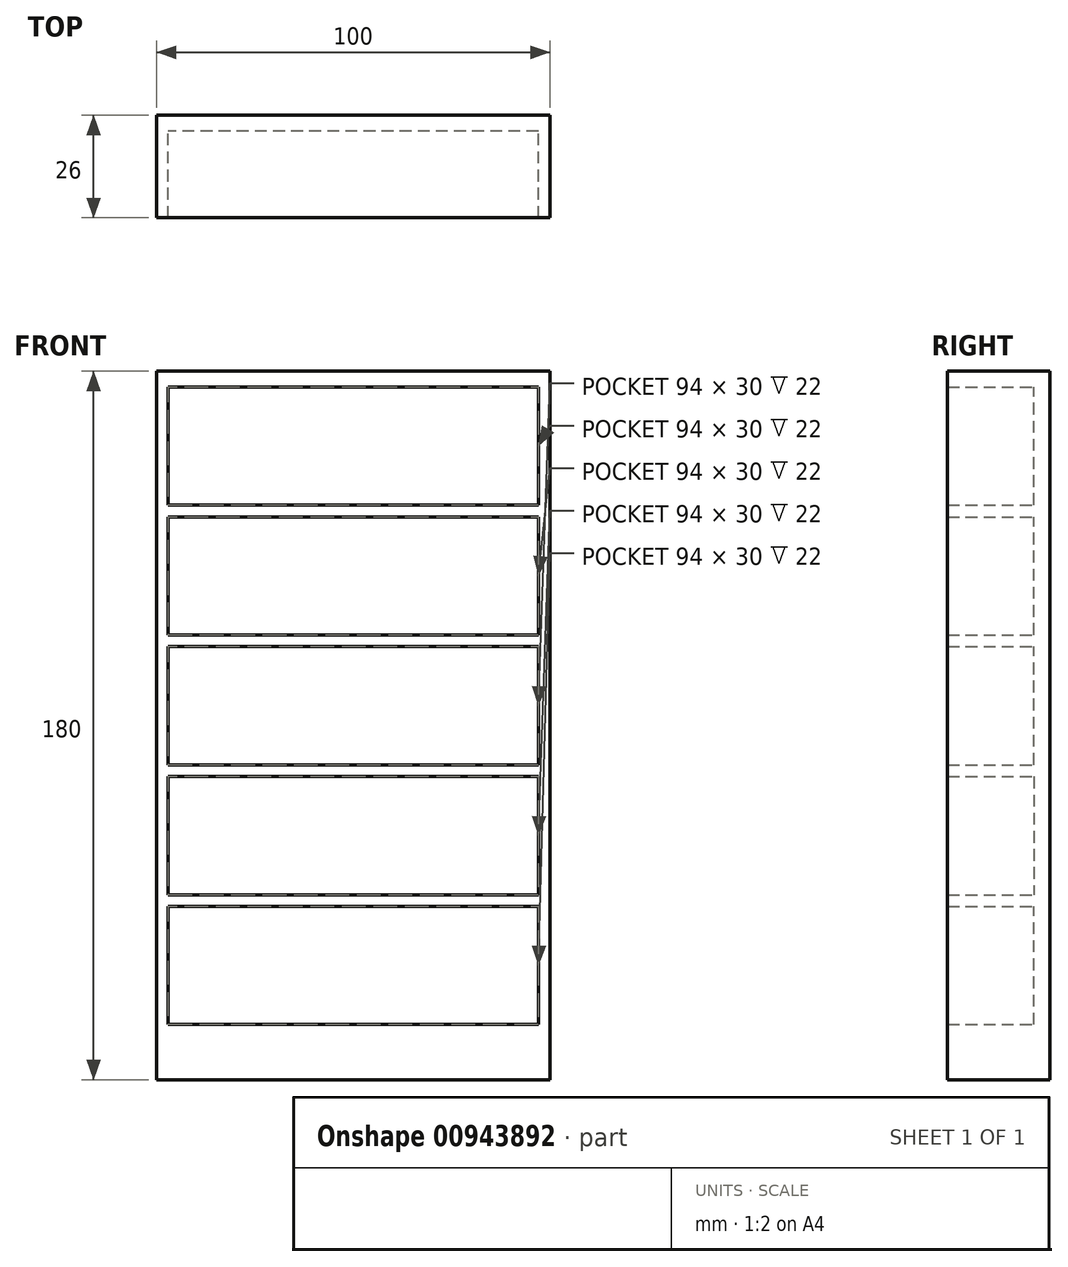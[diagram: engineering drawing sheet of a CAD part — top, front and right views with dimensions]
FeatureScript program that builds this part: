
annotation { "Feature Type Name" : "Feature", "Feature Type Description" : "" }
export const myFeature = defineFeature(function(context is Context, id is Id, definition is map)
    precondition{}
    {
        {
            var Q0;
            Q0=qCreatedBy(makeId("Front.planeOp"),FACE);
            var sketch = newSketch(context, id + "F0", { "sketchPlane" : qUnion([Q0])});
            skLineSegment(sketch, "E0.bottom", {"start": v(50, 90) * mm, "end": v(-50, 90) * mm});
            skLineSegment(sketch, "E0.top", {"start": v(50, -90) * mm, "end": v(-50, -90) * mm});
            skLineSegment(sketch, "E0.left", {"start": v(50, 90) * mm, "end": v(50, -90) * mm});
            skLineSegment(sketch, "E0.right", {"start": v(-50, 90) * mm, "end": v(-50, -90) * mm});
            skPoint(sketch, "E0.middle", {"position": v(0, 0) * mm});
            skLineSegment(sketch, "E1.bottom", {"start": v(-47, 86) * mm, "end": v(47, 86) * mm});
            skLineSegment(sketch, "E1.top", {"start": v(-47, 56) * mm, "end": v(47, 56) * mm});
            skLineSegment(sketch, "E1.left", {"start": v(-47, 86) * mm, "end": v(-47, 56) * mm});
            skLineSegment(sketch, "E1.right", {"start": v(47, 86) * mm, "end": v(47, 56) * mm});
            skLineSegment(sketch, "E2.bottom", {"start": v(-47, 53) * mm, "end": v(47, 53) * mm});
            skLineSegment(sketch, "E2.top", {"start": v(-47, 23) * mm, "end": v(47, 23) * mm});
            skLineSegment(sketch, "E2.left", {"start": v(-47, 53) * mm, "end": v(-47, 23) * mm});
            skLineSegment(sketch, "E2.right", {"start": v(47, 53) * mm, "end": v(47, 23) * mm});
            skLineSegment(sketch, "E3.bottom", {"start": v(-47, 20) * mm, "end": v(47, 20) * mm});
            skLineSegment(sketch, "E3.top", {"start": v(-47, -10) * mm, "end": v(47, -10) * mm});
            skLineSegment(sketch, "E3.left", {"start": v(47, 20) * mm, "end": v(47, -10) * mm});
            skLineSegment(sketch, "E3.right", {"start": v(-47, 20) * mm, "end": v(-47, -10) * mm});
            skLineSegment(sketch, "E4", {"start": v(-50, -11.5) * mm, "end": v(50, -11.5) * mm, "construction": true});
            skLineSegment(sketch, "E5.MirrorCS", {"start": v(47, -43) * mm, "end": v(47, -13) * mm});
            skLineSegment(sketch, "E6.MirrorCS", {"start": v(-47, -43) * mm, "end": v(47, -43) * mm});
            skLineSegment(sketch, "E7.MirrorCS", {"start": v(-47, -43) * mm, "end": v(-47, -13) * mm});
            skLineSegment(sketch, "E8.MirrorCS", {"start": v(-47, -13) * mm, "end": v(47, -13) * mm});
            skLineSegment(sketch, "E9", {"start": v(-50, -44.5) * mm, "end": v(50, -44.5) * mm, "construction": true});
            skLineSegment(sketch, "E10.MirrorCS", {"start": v(-47, -46) * mm, "end": v(-47, -76) * mm});
            skLineSegment(sketch, "E11.MirrorCS", {"start": v(-47, -76) * mm, "end": v(47, -76) * mm});
            skLineSegment(sketch, "E12.MirrorCS", {"start": v(47, -46) * mm, "end": v(47, -76) * mm});
            skLineSegment(sketch, "E13.MirrorCS", {"start": v(-47, -46) * mm, "end": v(47, -46) * mm});
            skSolve(sketch);
        }
        {
            var Q0;
            Q0 = qSketchRegion(id + "F0", true);
            var Q1;
            Q1=makeQuery(id+"F0.imprint","IMPRINT",FACE,{"disambiguationData":[TD([[makeQuery(id+"F0.imprint","IMPRINT",EDGE,{"derivedFrom":sQuery(id+"F0.wireOp",EDGE,"E1.bottom")}),-1.0]])]});
            var Q2;
            Q2=makeQuery(id+"F0.imprint","IMPRINT",FACE,{"disambiguationData":[TD([[makeQuery(id+"F0.imprint","IMPRINT",EDGE,{"derivedFrom":sQuery(id+"F0.wireOp",EDGE,"E2.bottom")}),-1.0]])]});
            var Q3;
            Q3=makeQuery(id+"F0.imprint","IMPRINT",FACE,{"disambiguationData":[TD([[makeQuery(id+"F0.imprint","IMPRINT",EDGE,{"derivedFrom":sQuery(id+"F0.wireOp",EDGE,"E3.bottom")}),-1.0]])]});
            var Q4;
            Q4=makeQuery(id+"F0.imprint","IMPRINT",FACE,{"disambiguationData":[TD([[makeQuery(id+"F0.imprint","IMPRINT",EDGE,{"derivedFrom":sQuery(id+"F0.wireOp",EDGE,"E5.MirrorCS")}),1.0]])]});
            var Q5;
            Q5=makeQuery(id+"F0.imprint","IMPRINT",FACE,{"disambiguationData":[TD([[makeQuery(id+"F0.imprint","IMPRINT",EDGE,{"derivedFrom":sQuery(id+"F0.wireOp",EDGE,"E10.MirrorCS")}),1.0]])]});
            extrude(context, id + "F1", {"entities" : qUnion([Q0, Q1, Q2, Q3, Q4, Q5]), "depth" : 4 * mm, "offsetDistance" : 25 * mm});
        }
        {
            var Q0;
            Q0 = qSketchRegion(id + "F0", true);
            extrude(context, id + "F2", {"entities" : qUnion([Q0]), "operationType" : NewBodyOperationType.ADD, "depth" : 26 * mm, "offsetDistance" : 25 * mm});
        }
    });
